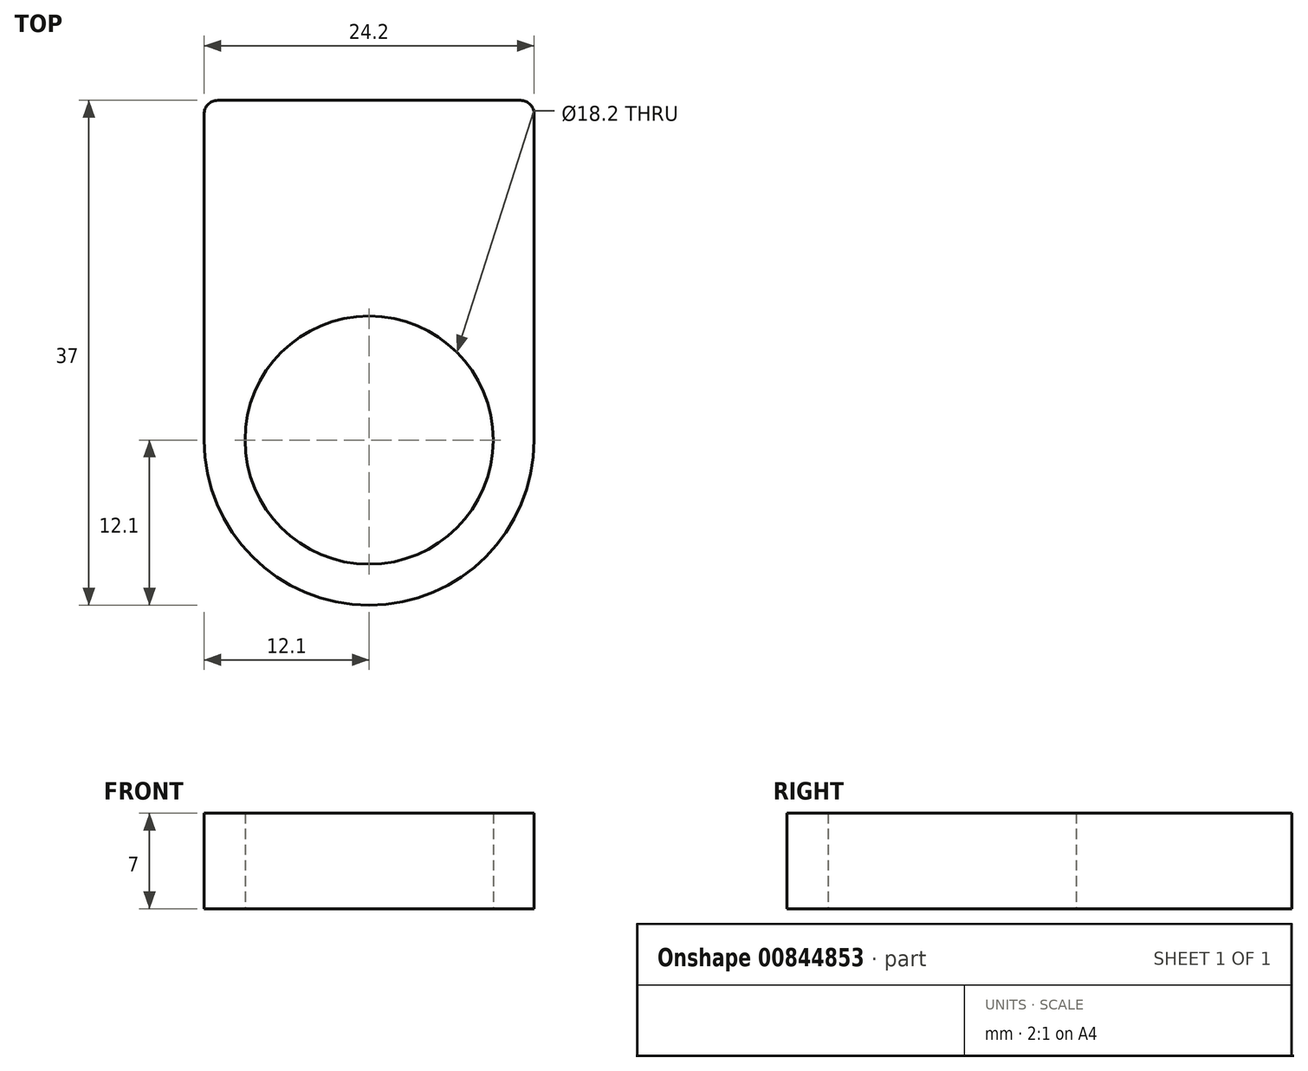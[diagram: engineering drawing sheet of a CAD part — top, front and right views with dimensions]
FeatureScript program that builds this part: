
annotation { "Feature Type Name" : "Feature", "Feature Type Description" : "" }
export const myFeature = defineFeature(function(context is Context, id is Id, definition is map)
    precondition{}
    {
        {
            var Q0;
            Q0=qCreatedBy(makeId("Top.planeOp"),FACE);
            var sketch = newSketch(context, id + "F0", { "sketchPlane" : qUnion([Q0])});
            skCircle(sketch, "E0", {"center": v(0, 0) * mm, "radius": 9.1 * mm});
            skCircle(sketch, "E1", {"center": v(0, 0) * mm, "radius": 12.1 * mm});
            skLineSegment(sketch, "E2", {"start": v(12.1, 0) * mm, "end": v(12.1, 24.9) * mm});
            skLineSegment(sketch, "E3", {"start": v(-12.1, 0) * mm, "end": v(-12.1, 24.9) * mm});
            skLineSegment(sketch, "E4", {"start": v(-12.1, 24.9) * mm, "end": v(12.1, 24.9) * mm});
            skSolve(sketch);
        }
        {
            var Q0;
            Q0 = qSketchRegion(id + "F0", true);
            extrude(context, id + "F1", {"entities" : qUnion([Q0]), "depth" : 7 * mm, "offsetDistance" : 25 * mm});
        }
        {
            var Q0;
            Q0=makeQuery(id+"F1.opExtrude","SWEPT_EDGE",EDGE,{"disambiguationData":[OSD([sQuery(id+"F0.wireOp",EDGE,"E3"),sQuery(id+"F0.wireOp",EDGE,"E4")])]});
            fillet(context, id + "F2", {"entities" : qUnion([Q0]), "radius" : 1 * mm, "tangentPropagation" : true, "allowEdgeOverflow" : false});
        }
        {
            var Q0;
            Q0=makeQuery(id+"F1.opExtrude","SWEPT_EDGE",EDGE,{"disambiguationData":[OSD([sQuery(id+"F0.wireOp",EDGE,"E2"),sQuery(id+"F0.wireOp",EDGE,"E4")])]});
            fillet(context, id + "F3", {"entities" : qUnion([Q0]), "radius" : 1 * mm, "tangentPropagation" : true, "allowEdgeOverflow" : false});
        }
    });
